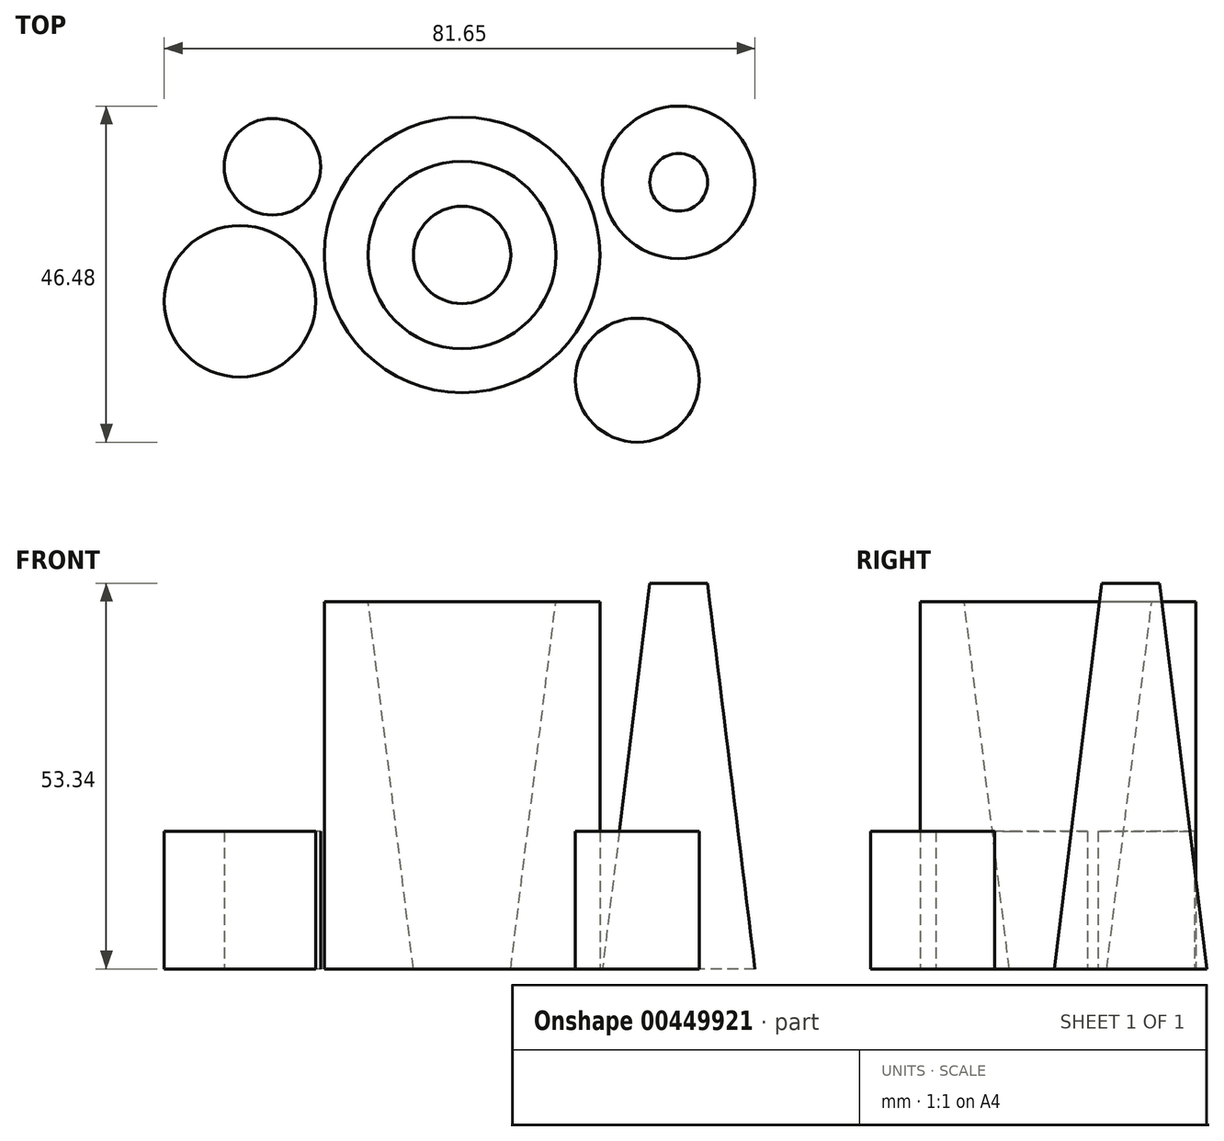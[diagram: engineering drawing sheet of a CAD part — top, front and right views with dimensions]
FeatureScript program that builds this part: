
annotation { "Feature Type Name" : "Feature", "Feature Type Description" : "" }
export const myFeature = defineFeature(function(context is Context, id is Id, definition is map)
    precondition{}
    {
        {
            var Q0;
            Q0=qCreatedBy(makeId("Top.planeOp"),FACE);
            var sketch = newSketch(context, id + "F0", { "sketchPlane" : qUnion([Q0])});
            skCircle(sketch, "E0", {"center": v(0, 0) * mm, "radius": 19.05 * mm});
            skSolve(sketch);
        }
        {
            var Q0;
            Q0 = qSketchRegion(id + "F0", true);
            extrude(context, id + "F1", {"entities" : qUnion([Q0]), "depth" : 50.8 * mm});
        }
        {
            var Q0;
            Q0=makeQuery(id+"F1.opExtrude","CAP_FACE",FACE,{"disambiguationData":[OSD([sQuery(id+"F0.wireOp",EDGE,"E0")])],"isStart":false});
            var sketch = newSketch(context, id + "F2", { "sketchPlane" : qUnion([Q0])});
            skCircle(sketch, "E1", {"center": v(0, 0) * mm, "radius": 12.97 * mm});
            skSolve(sketch);
        }
        {
            var Q0;
            Q0 = qSketchRegion(id + "F2", true);
            extrude(context, id + "F3", {"entities" : qUnion([Q0]), "operationType" : NewBodyOperationType.REMOVE, "endBound" : BoundingType.THROUGH_ALL, "oppositeDirection" : true, "depth" : 25.4 * mm, "hasDraft" : true, "draftAngle" : 7 * degree, "draftPullDirection" : true});
        }
        {
            var Q0;
            Q0=qCreatedBy(makeId("Top.planeOp"),FACE);
            var sketch = newSketch(context, id + "F4", { "sketchPlane" : qUnion([Q0])});
            skCircle(sketch, "E2", {"center": v(-26.21, 12.2) * mm, "radius": 6.67 * mm});
            skSolve(sketch);
        }
        {
            var Q0;
            Q0=makeQuery(id+"F4.imprint","IMPRINT",FACE,{"disambiguationData":[TD([[makeQuery(id+"F4.imprint","IMPRINT",EDGE,{"derivedFrom":sQuery(id+"F4.wireOp",EDGE,"E2")}),1.0]])]});
            extrude(context, id + "F5", {"entities" : qUnion([Q0]), "depth" : 19.05 * mm});
        }
        {
            var Q0;
            Q0=qCreatedBy(makeId("Top.planeOp"),FACE);
            var sketch = newSketch(context, id + "F6", { "sketchPlane" : qUnion([Q0])});
            skCircle(sketch, "E3", {"center": v(24.22, -17.32) * mm, "radius": 8.57 * mm});
            skSolve(sketch);
        }
        {
            var Q0;
            Q0=makeQuery(id+"F6.imprint","IMPRINT",FACE,{"disambiguationData":[TD([[makeQuery(id+"F6.imprint","IMPRINT",EDGE,{"derivedFrom":sQuery(id+"F6.wireOp",EDGE,"E3")}),1.0]])]});
            extrude(context, id + "F7", {"entities" : qUnion([Q0]), "depth" : 19.05 * mm});
        }
        {
            var Q0;
            Q0=qCreatedBy(makeId("Top.planeOp"),FACE);
            var sketch = newSketch(context, id + "F8", { "sketchPlane" : qUnion([Q0])});
            skCircle(sketch, "E4", {"center": v(-30.69, -6.4) * mm, "radius": 10.48 * mm});
            skSolve(sketch);
        }
        {
            var Q0;
            Q0=makeQuery(id+"F8.imprint","IMPRINT",FACE,{"disambiguationData":[TD([[makeQuery(id+"F8.imprint","IMPRINT",EDGE,{"derivedFrom":sQuery(id+"F8.wireOp",EDGE,"E4")}),1.0]])]});
            extrude(context, id + "F9", {"entities" : qUnion([Q0]), "depth" : 19.05 * mm});
        }
        {
            var Q0;
            Q0=qCreatedBy(makeId("Top.planeOp"),FACE);
            var sketch = newSketch(context, id + "F10", { "sketchPlane" : qUnion([Q0])});
            skCircle(sketch, "E5", {"center": v(29.94, 10.05) * mm, "radius": 10.54 * mm});
            skSolve(sketch);
        }
        {
            var Q0;
            Q0=makeQuery(id+"F10.imprint","IMPRINT",FACE,{"disambiguationData":[TD([[makeQuery(id+"F10.imprint","IMPRINT",EDGE,{"derivedFrom":sQuery(id+"F10.wireOp",EDGE,"E5")}),1.0]])]});
            extrude(context, id + "F11", {"entities" : qUnion([Q0]), "depth" : 53.34 * mm, "hasDraft" : true, "draftAngle" : 7 * degree, "draftPullDirection" : true});
        }
    });
